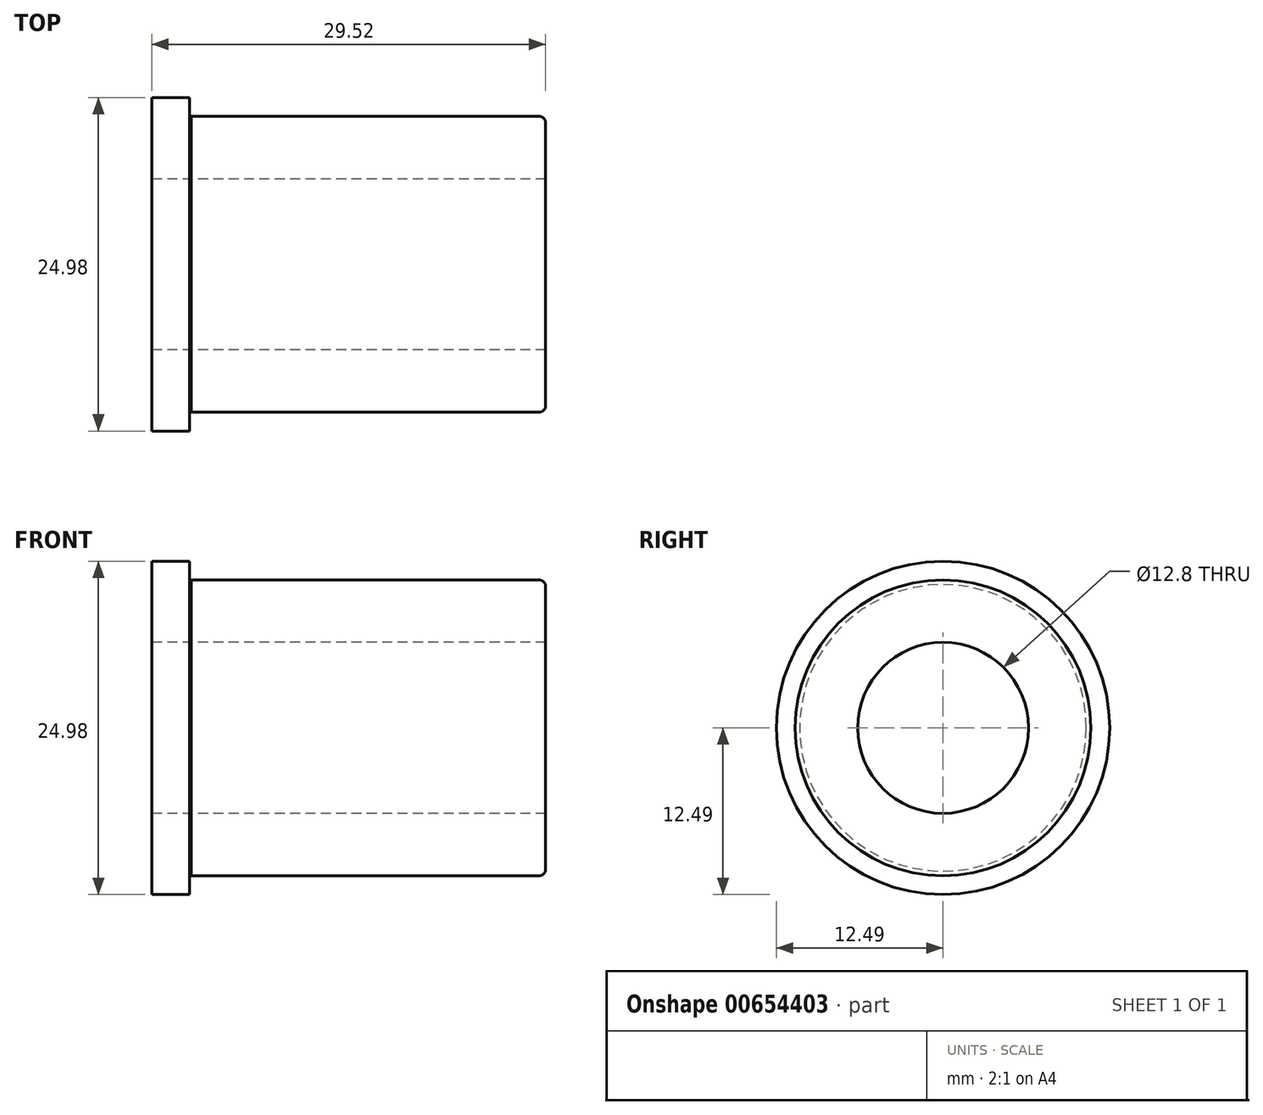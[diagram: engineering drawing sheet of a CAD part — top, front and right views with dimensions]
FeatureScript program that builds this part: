
annotation { "Feature Type Name" : "Feature", "Feature Type Description" : "" }
export const myFeature = defineFeature(function(context is Context, id is Id, definition is map)
    precondition{}
    {
        {
            var Q0;
            Q0=qCreatedBy(makeId("Right.planeOp"),FACE);
            var sketch = newSketch(context, id + "F0", { "sketchPlane" : qUnion([Q0])});
            skCircle(sketch, "E0", {"center": v(0, 0) * mm, "radius": 12.5 * mm});
            skSolve(sketch);
        }
        {
            var Q0;
            Q0=makeQuery(id+"F0.imprint","IMPRINT",FACE,{"disambiguationData":[TD([[makeQuery(id+"F0.imprint","IMPRINT",EDGE,{"derivedFrom":sQuery(id+"F0.wireOp",EDGE,"E0")}),1.0]])]});
            extrude(context, id + "F1", {"entities" : qUnion([Q0]), "depth" : 2.84 * mm, "offsetDistance" : 25 * mm});
        }
        {
            var Q0;
            Q0=makeQuery(id+"F1.opExtrude","CAP_FACE",FACE,{"disambiguationData":[OSD([sQuery(id+"F0.wireOp",EDGE,"E0")])],"isStart":false});
            var sketch = newSketch(context, id + "F2", { "sketchPlane" : qUnion([Q0])});
            skCircle(sketch, "E1", {"center": v(0, 0) * mm, "radius": 10.74 * mm});
            skSolve(sketch);
        }
        {
            var Q0;
            Q0=makeQuery(id+"F2.imprint","IMPRINT",FACE,{"disambiguationData":[TD([[makeQuery(id+"F2.imprint","IMPRINT",EDGE,{"derivedFrom":sQuery(id+"F2.wireOp",EDGE,"E1")}),1.0]])]});
            extrude(context, id + "F3", {"entities" : qUnion([Q0]), "operationType" : NewBodyOperationType.ADD, "depth" : 0.12 * mm, "offsetDistance" : 25 * mm});
        }
        {
            var Q0;
            Q0=makeQuery(id+"F3.opExtrude","CAP_FACE",FACE,{"disambiguationData":[OSD([sQuery(id+"F2.wireOp",EDGE,"E1")])],"isStart":false});
            var sketch = newSketch(context, id + "F4", { "sketchPlane" : qUnion([Q0])});
            skCircle(sketch, "E2", {"center": v(0, 0) * mm, "radius": 11.08 * mm});
            skSolve(sketch);
        }
        {
            var Q0;
            Q0=qSketchRegion(id+"F4",true);
            extrude(context, id + "F5", {"entities" : qUnion([Q0]), "operationType" : NewBodyOperationType.ADD, "depth" : 26.56 * mm, "offsetDistance" : 25 * mm});
        }
        {
            var Q0;
            Q0=makeQuery(id+"F1.opExtrude","CAP_FACE",FACE,{"disambiguationData":[OSD([sQuery(id+"F0.wireOp",EDGE,"E0")])],"isStart":true});
            var sketch = newSketch(context, id + "F6", { "sketchPlane" : qUnion([Q0])});
            skCircle(sketch, "E3", {"center": v(0, 0) * mm, "radius": 6.4 * mm});
            skSolve(sketch);
        }
        {
            var Q0;
            Q0=makeQuery(id+"F6.imprint","IMPRINT",FACE,{"disambiguationData":[TD([[makeQuery(id+"F6.imprint","IMPRINT",EDGE,{"derivedFrom":sQuery(id+"F6.wireOp",EDGE,"E3")}),1.0]])]});
            extrude(context, id + "F7", {"entities" : qUnion([Q0]), "operationType" : NewBodyOperationType.REMOVE, "oppositeDirection" : true, "depth" : 29.52 * mm, "offsetDistance" : 25 * mm});
        }
        {
            var Q0;
            Q0=makeQuery(id+"F7.boolean.opBoolean","COPY",EDGE,{"derivedFrom":makeQuery(id+"F7.opExtrude","CAP_EDGE",EDGE,{"disambiguationData":[OSD([sQuery(id+"F6.wireOp",EDGE,"E3")])],"isStart":true})});
            var Q1;
            Q1=makeQuery(id+"F5.opExtrude","CAP_EDGE",EDGE,{"disambiguationData":[OSD([sQuery(id+"F4.wireOp",EDGE,"E2")])],"isStart":false});
            var Q2;
            Q2=makeQuery(id+"F7.boolean.opBoolean","COPY",EDGE,{"derivedFrom":makeQuery(id+"F7.opExtrude","CAP_EDGE",EDGE,{"disambiguationData":[OSD([sQuery(id+"F6.wireOp",EDGE,"E3")])],"isStart":false})});
            fillet(context, id + "F8", {"entities" : qUnion([Q0, Q1, Q2]), "radius" : 0.5 * mm, "tangentPropagation" : true, "allowEdgeOverflow" : false});
        }
    });
